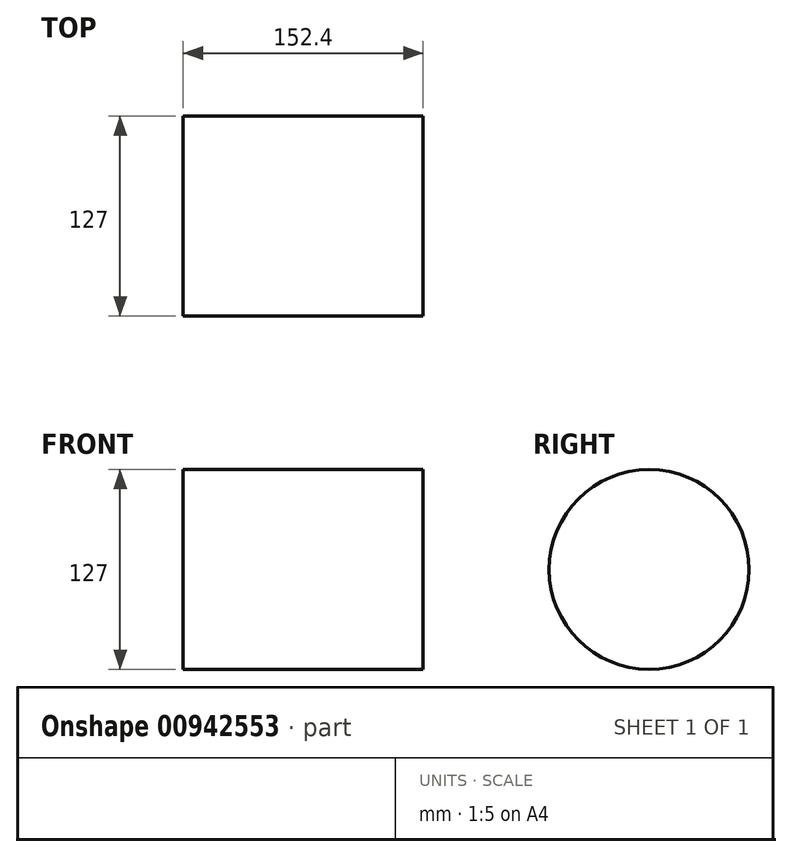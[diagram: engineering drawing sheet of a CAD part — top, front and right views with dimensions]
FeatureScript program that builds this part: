
annotation { "Feature Type Name" : "Feature", "Feature Type Description" : "" }
export const myFeature = defineFeature(function(context is Context, id is Id, definition is map)
    precondition{}
    {
        {
            var Q0;
            Q0=qCreatedBy(makeId("Right.planeOp"),FACE);
            var sketch = newSketch(context, id + "F0", { "sketchPlane" : qUnion([Q0])});
            skCircle(sketch, "E0", {"center": v(0, 0) * mm, "radius": 63.5 * mm});
            skSolve(sketch);
        }
        {
            var Q0;
            Q0=makeQuery(id+"F0.imprint","IMPRINT",FACE,{"disambiguationData":[TD([[makeQuery(id+"F0.imprint","IMPRINT",EDGE,{"derivedFrom":sQuery(id+"F0.wireOp",EDGE,"E0")}),1.0]])]});
            extrude(context, id + "F1", {"entities" : qUnion([Q0]), "depth" : 152.4 * mm, "offsetDistance" : 25.4 * mm});
        }
    });
